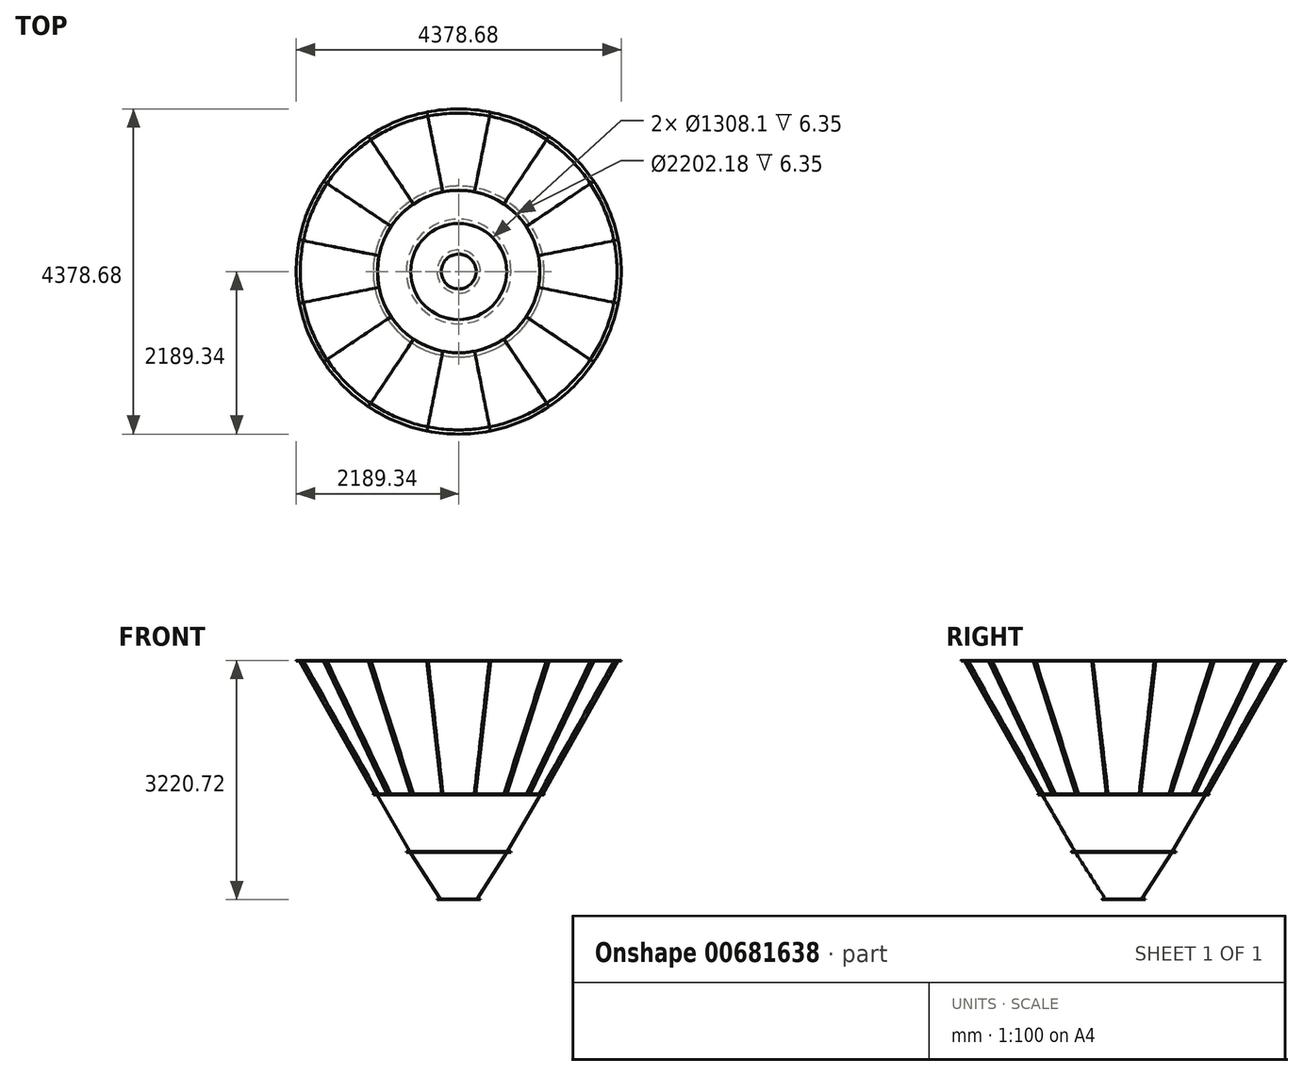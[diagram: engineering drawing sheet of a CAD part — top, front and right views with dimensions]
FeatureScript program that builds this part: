
annotation { "Feature Type Name" : "Feature", "Feature Type Description" : "" }
export const myFeature = defineFeature(function(context is Context, id is Id, definition is map)
    precondition{}
    {
        {
            var Q0;
            Q0=qCreatedBy(makeId("Top.planeOp"),FACE);
            var sketch = newSketch(context, id + "F0", { "sketchPlane" : qUnion([Q0])});
            skCircle(sketch, "E0", {"center": v(0, 0) * mm, "radius": 2133.6 * mm, "construction": true});
            skCircle(sketch, "E1", {"center": v(0, 0) * mm, "radius": 2139.95 * mm, "construction": true});
            skLineSegment(sketch, "E2", {"start": v(0, 0) * mm, "end": v(0, -2304.22) * mm});
            skLineSegment(sketch, "E3", {"start": v(0, -2304.22) * mm, "end": v(0, 0) * mm, "construction": true});
            skLineSegment(sketch, "E4", {"start": v(0, 0) * mm, "end": v(2542.21, 0) * mm, "construction": true});
            skLineSegment(sketch, "E5", {"start": v(0, 0) * mm, "end": v(1217.12, -1821.54) * mm, "construction": true});
            skLineSegment(sketch, "E6", {"start": v(0, 0) * mm, "end": v(1821.54, -1217.12) * mm, "construction": true});
            skLineSegment(sketch, "E7", {"start": v(1217.12, -1821.54) * mm, "end": v(1185.36, -1774.02) * mm});
            skLineSegment(sketch, "E8", {"start": v(1217.12, -1821.54) * mm, "end": v(1222.4, -1818.01) * mm});
            skLineSegment(sketch, "E9", {"start": v(1821.54, -1217.12) * mm, "end": v(1774.02, -1185.36) * mm});
            skLineSegment(sketch, "E10", {"start": v(1821.54, -1217.12) * mm, "end": v(1818.01, -1222.4) * mm});
            skArc(sketch, "E11", {"start": v(1185.36, -1774.02) * mm, "mid": v(1508.68, -1508.68) * mm, "end": v(1774.02, -1185.36) * mm});
            skLineSegment(sketch, "E12", {"start": v(1222.4, -1818.01) * mm, "end": v(1194.17, -1775.77) * mm});
            skLineSegment(sketch, "E13", {"start": v(1818.01, -1222.4) * mm, "end": v(1775.77, -1194.17) * mm});
            skArc(sketch, "E14", {"start": v(1194.17, -1775.77) * mm, "mid": v(1513.17, -1513.17) * mm, "end": v(1775.77, -1194.17) * mm});
            skLineSegment(sketch, "E15", {"start": v(0, 0) * mm, "end": v(2368.08, -471.04) * mm, "construction": true});
            skLineSegment(sketch, "E16", {"start": v(0, 0) * mm, "end": v(2425.64, 482.49) * mm, "construction": true});
            skLineSegment(sketch, "E17", {"start": v(0, 0) * mm, "end": v(2044.18, 1365.87) * mm, "construction": true});
            skLineSegment(sketch, "E18", {"start": v(0, 0) * mm, "end": v(1324.45, 1982.17) * mm, "construction": true});
            skLineSegment(sketch, "E19", {"start": v(0, 0) * mm, "end": v(473.22, 2379.02) * mm, "construction": true});
            skLineSegment(sketch, "E20", {"start": v(0, 0) * mm, "end": v(-472.95, 2377.66) * mm, "construction": true});
            skSolve(sketch);
        }
        {
            var Q0;
            Q0=qCreatedBy(makeId("Front.planeOp"),FACE);
            var sketch = newSketch(context, id + "F1", { "sketchPlane" : qUnion([Q0])});
            skLineSegment(sketch, "E21", {"start": v(0, 0) * mm, "end": v(0, -1803.4) * mm, "construction": true});
            skLineSegment(sketch, "E22", {"start": v(0, -1803.4) * mm, "end": v(0, -2578.1) * mm, "construction": true});
            skLineSegment(sketch, "E23", {"start": v(0, -2578.1) * mm, "end": v(0, -3220.72) * mm, "construction": true});
            skLineSegment(sketch, "E24", {"start": v(0, -1803.4) * mm, "end": v(-1101.72, -1803.4) * mm, "construction": true});
            skLineSegment(sketch, "E25", {"start": v(0, -1803.4) * mm, "end": v(1101.73, -1803.4) * mm, "construction": true});
            skLineSegment(sketch, "E26", {"start": v(0, -2578.1) * mm, "end": v(-475.6, -2578.1) * mm, "construction": true});
            skLineSegment(sketch, "E27", {"start": v(0, -3220.72) * mm, "end": v(-292.1, -3220.72) * mm, "construction": true});
            skSolve(sketch);
        }
        {
            var Q0;
            Q0=sQuery(id+"F1.wireOp",EDGE,"E25");
            cPlane(context, id + "F2", {"entities" : qUnion([Q0]), "cplaneType" : CPlaneType.LINE_ANGLE, "offset" : 25.4 * mm, "angle" : 90 * degree, "width" : 152.4 * mm, "height" : 152.4 * mm});
        }
        {
            var Q0;
            Q0=qCreatedBy(id+"F2.planeOp",FACE);
            var sketch = newSketch(context, id + "F3", { "sketchPlane" : qUnion([Q0])});
            skCircle(sketch, "E28", {"center": v(0, 0) * mm, "radius": 1151.9 * mm, "construction": true});
            skLineSegment(sketch, "E29", {"start": v(640.06, -957.7) * mm, "end": v(608.74, -911.75) * mm});
            skLineSegment(sketch, "E30", {"start": v(640.06, -957.7) * mm, "end": v(645.3, -954.12) * mm});
            skLineSegment(sketch, "E31", {"start": v(957.75, -639.98) * mm, "end": v(911.58, -609) * mm});
            skLineSegment(sketch, "E32", {"start": v(957.75, -639.98) * mm, "end": v(954.2, -645.6) * mm});
            skArc(sketch, "E33", {"start": v(608.74, -911.75) * mm, "mid": v(775.09, -775.3) * mm, "end": v(911.58, -609) * mm});
            skLineSegment(sketch, "E34", {"start": v(954.2, -645.6) * mm, "end": v(913.11, -618.03) * mm});
            skLineSegment(sketch, "E35", {"start": v(645.3, -954.12) * mm, "end": v(617.57, -913.42) * mm});
            skArc(sketch, "E36", {"start": v(617.57, -913.42) * mm, "mid": v(779.46, -779.85) * mm, "end": v(913.11, -618.03) * mm});
            skSolve(sketch);
        }
        {
            var Q0;
            Q0=makeQuery(id+"F3.imprint","IMPRINT",FACE,{"disambiguationData":[TD([[makeQuery(id+"F3.imprint","IMPRINT",EDGE,{"derivedFrom":sQuery(id+"F3.wireOp",EDGE,"E29")}),-1.0]])]});
            var Q1;
            Q1=makeQuery(id+"F0.imprint","IMPRINT",FACE,{"disambiguationData":[TD([[makeQuery(id+"F0.imprint","IMPRINT",EDGE,{"derivedFrom":sQuery(id+"F0.wireOp",EDGE,"E7")}),-1.0]])]});
            loft(context, id + "F4", {"sheetProfilesArray" : [{ "sheetProfileEntities" : qUnion([Q0]) }, { "sheetProfileEntities" : qUnion([Q1]) }]});
        }
        {
            var Q0;
            Q0=qCreatedBy(makeId("Top.planeOp"),FACE);
            var sketch = newSketch(context, id + "F5", { "sketchPlane" : qUnion([Q0])});
            skArc(sketch, "E37", {"start": v(1185.3, -1774.06) * mm, "mid": v(1508.65, -1508.72) * mm, "end": v(1774, -1185.39) * mm});
            skLineSegment(sketch, "E38", {"start": v(1185.3, -1774.06) * mm, "end": v(1216.33, -1820.37) * mm});
            skLineSegment(sketch, "E39", {"start": v(1774, -1185.39) * mm, "end": v(1820.44, -1216.23) * mm});
            skArc(sketch, "E40", {"start": v(1216.33, -1820.37) * mm, "mid": v(1548.14, -1548.05) * mm, "end": v(1820.44, -1216.23) * mm});
            skSolve(sketch);
        }
        {
            var Q0;
            Q0=makeQuery(id+"F5.imprint","IMPRINT",FACE,{"disambiguationData":[TD([[makeQuery(id+"F5.imprint","IMPRINT",EDGE,{"derivedFrom":sQuery(id+"F5.wireOp",EDGE,"E37")}),-1.0]])]});
            extrude(context, id + "F6", {"entities" : qUnion([Q0]), "operationType" : NewBodyOperationType.ADD, "oppositeDirection" : true, "depth" : 6.35 * mm, "offsetDistance" : 25.4 * mm});
        }
        {
            var Q0;
            Q0=qCreatedBy(id+"F2.planeOp",FACE);
            var sketch = newSketch(context, id + "F7", { "sketchPlane" : qUnion([Q0])});
            skArc(sketch, "E41", {"start": v(607.56, -909.75) * mm, "mid": v(773.48, -773.63) * mm, "end": v(909.63, -607.74) * mm});
            skArc(sketch, "E42", {"start": v(640.03, -957.7) * mm, "mid": v(814.54, -814.48) * mm, "end": v(957.76, -639.96) * mm});
            skLineSegment(sketch, "E43", {"start": v(607.56, -909.75) * mm, "end": v(640.03, -957.7) * mm});
            skLineSegment(sketch, "E44", {"start": v(909.63, -607.74) * mm, "end": v(957.76, -639.96) * mm});
            skSolve(sketch);
        }
        {
            var Q0;
            Q0 = qSketchRegion(id + "F7", true);
            extrude(context, id + "F8", {"entities" : qUnion([Q0]), "depth" : 6.35 * mm, "offsetDistance" : 25.4 * mm});
        }
        {
            var Q0;
            Q0=sQuery(id+"F0.wireOp",EDGE,"E5");
            cPlane(context, id + "F9", {"entities" : qUnion([Q0]), "cplaneType" : CPlaneType.LINE_ANGLE, "offset" : 25.4 * mm, "angle" : 90 * degree, "width" : 152.4 * mm, "height" : 152.4 * mm});
        }
        {
            var Q0;
            Q0=makeQuery(id+"F4.opLoft","SWEPT_BODY",BODY,{"disambiguationData":[OSD([makeQuery(id+"F0.imprint","IMPRINT",FACE,{"disambiguationData":[TD([[makeQuery(id+"F0.imprint","IMPRINT",EDGE,{"derivedFrom":sQuery(id+"F0.wireOp",EDGE,"E7")}),-1.0]])]}),makeQuery(id+"F3.imprint","IMPRINT",FACE,{"disambiguationData":[TD([[makeQuery(id+"F3.imprint","IMPRINT",EDGE,{"derivedFrom":sQuery(id+"F3.wireOp",EDGE,"E29")}),-1.0]])]})])]});
            var Q1;
            Q1=makeQuery(id+"F8.opExtrude","SWEPT_BODY",BODY,{"disambiguationData":[OSD([sQuery(id+"F7.wireOp",EDGE,"E41"),sQuery(id+"F7.wireOp",EDGE,"E42"),sQuery(id+"F7.wireOp",EDGE,"E43"),sQuery(id+"F7.wireOp",EDGE,"E44")])]});
            var Q2;
            Q2=qCreatedBy(id+"F9.planeOp",FACE);
            mirror(context, id + "F10", {"entities" : qUnion([Q0, Q1]), "mirrorPlane" : qUnion([Q2])});
        }
        {
            var Q0;
            Q0=sQuery(id+"F0.wireOp",EDGE,"E6");
            cPlane(context, id + "F11", {"entities" : qUnion([Q0]), "cplaneType" : CPlaneType.LINE_ANGLE, "offset" : 25.4 * mm, "angle" : 0 * degree, "width" : 152.4 * mm, "height" : 152.4 * mm});
        }
        {
            var Q0;
            Q0=makeQuery(id+"F4.opLoft","SWEPT_BODY",BODY,{"disambiguationData":[OSD([makeQuery(id+"F0.imprint","IMPRINT",FACE,{"disambiguationData":[TD([[makeQuery(id+"F0.imprint","IMPRINT",EDGE,{"derivedFrom":sQuery(id+"F0.wireOp",EDGE,"E7")}),-1.0]])]}),makeQuery(id+"F3.imprint","IMPRINT",FACE,{"disambiguationData":[TD([[makeQuery(id+"F3.imprint","IMPRINT",EDGE,{"derivedFrom":sQuery(id+"F3.wireOp",EDGE,"E29")}),-1.0]])]})])]});
            var Q1;
            Q1=makeQuery(id+"F8.opExtrude","SWEPT_BODY",BODY,{"disambiguationData":[OSD([sQuery(id+"F7.wireOp",EDGE,"E41"),sQuery(id+"F7.wireOp",EDGE,"E42"),sQuery(id+"F7.wireOp",EDGE,"E43"),sQuery(id+"F7.wireOp",EDGE,"E44")])]});
            var Q2;
            Q2=qCreatedBy(id+"F11.planeOp",FACE);
            mirror(context, id + "F12", {"entities" : qUnion([Q0, Q1]), "mirrorPlane" : qUnion([Q2])});
        }
        {
            var Q0;
            Q0=sQuery(id+"F0.wireOp",EDGE,"E15");
            cPlane(context, id + "F13", {"entities" : qUnion([Q0]), "cplaneType" : CPlaneType.LINE_ANGLE, "offset" : 25.4 * mm, "angle" : 0 * degree, "width" : 152.4 * mm, "height" : 152.4 * mm});
        }
        {
            var Q0;
            Q0=sQuery(id+"F0.wireOp",EDGE,"E16");
            cPlane(context, id + "F14", {"entities" : qUnion([Q0]), "cplaneType" : CPlaneType.LINE_ANGLE, "offset" : 25.4 * mm, "angle" : 0 * degree, "width" : 152.4 * mm, "height" : 152.4 * mm});
        }
        {
            var Q0;
            Q0=sQuery(id+"F0.wireOp",EDGE,"E17");
            cPlane(context, id + "F15", {"entities" : qUnion([Q0]), "cplaneType" : CPlaneType.LINE_ANGLE, "offset" : 25.4 * mm, "angle" : 0 * degree, "width" : 152.4 * mm, "height" : 152.4 * mm});
        }
        {
            var Q0;
            Q0=makeQuery(id+"F12.opPattern","COPY",BODY,{"derivedFrom":makeQuery(id+"F4.opLoft","SWEPT_BODY",BODY,{"disambiguationData":[OSD([makeQuery(id+"F0.imprint","IMPRINT",FACE,{"disambiguationData":[TD([[makeQuery(id+"F0.imprint","IMPRINT",EDGE,{"derivedFrom":sQuery(id+"F0.wireOp",EDGE,"E7")}),-1.0]])]}),makeQuery(id+"F3.imprint","IMPRINT",FACE,{"disambiguationData":[TD([[makeQuery(id+"F3.imprint","IMPRINT",EDGE,{"derivedFrom":sQuery(id+"F3.wireOp",EDGE,"E29")}),-1.0]])]})])]}),"instanceName":"1"});
            var Q1;
            Q1=makeQuery(id+"F12.opPattern","COPY",BODY,{"derivedFrom":makeQuery(id+"F8.opExtrude","SWEPT_BODY",BODY,{"disambiguationData":[OSD([sQuery(id+"F7.wireOp",EDGE,"E41"),sQuery(id+"F7.wireOp",EDGE,"E42"),sQuery(id+"F7.wireOp",EDGE,"E43"),sQuery(id+"F7.wireOp",EDGE,"E44")])]}),"instanceName":"1"});
            var Q2;
            Q2=qCreatedBy(id+"F13.planeOp",FACE);
            mirror(context, id + "F16", {"entities" : qUnion([Q0, Q1]), "mirrorPlane" : qUnion([Q2])});
        }
        {
            var Q0;
            Q0=makeQuery(id+"F16.opPattern","COPY",BODY,{"derivedFrom":makeQuery(id+"F12.opPattern","COPY",BODY,{"derivedFrom":makeQuery(id+"F4.opLoft","SWEPT_BODY",BODY,{"disambiguationData":[OSD([makeQuery(id+"F0.imprint","IMPRINT",FACE,{"disambiguationData":[TD([[makeQuery(id+"F0.imprint","IMPRINT",EDGE,{"derivedFrom":sQuery(id+"F0.wireOp",EDGE,"E7")}),-1.0]])]}),makeQuery(id+"F3.imprint","IMPRINT",FACE,{"disambiguationData":[TD([[makeQuery(id+"F3.imprint","IMPRINT",EDGE,{"derivedFrom":sQuery(id+"F3.wireOp",EDGE,"E29")}),-1.0]])]})])]}),"instanceName":"1"}),"instanceName":"1"});
            var Q1;
            Q1=makeQuery(id+"F16.opPattern","COPY",BODY,{"derivedFrom":makeQuery(id+"F12.opPattern","COPY",BODY,{"derivedFrom":makeQuery(id+"F8.opExtrude","SWEPT_BODY",BODY,{"disambiguationData":[OSD([sQuery(id+"F7.wireOp",EDGE,"E41"),sQuery(id+"F7.wireOp",EDGE,"E42"),sQuery(id+"F7.wireOp",EDGE,"E43"),sQuery(id+"F7.wireOp",EDGE,"E44")])]}),"instanceName":"1"}),"instanceName":"1"});
            var Q2;
            Q2=qCreatedBy(id+"F14.planeOp",FACE);
            mirror(context, id + "F17", {"entities" : qUnion([Q0, Q1]), "mirrorPlane" : qUnion([Q2])});
        }
        {
            var Q0;
            Q0=makeQuery(id+"F17.opPattern","COPY",BODY,{"derivedFrom":makeQuery(id+"F16.opPattern","COPY",BODY,{"derivedFrom":makeQuery(id+"F12.opPattern","COPY",BODY,{"derivedFrom":makeQuery(id+"F4.opLoft","SWEPT_BODY",BODY,{"disambiguationData":[OSD([makeQuery(id+"F0.imprint","IMPRINT",FACE,{"disambiguationData":[TD([[makeQuery(id+"F0.imprint","IMPRINT",EDGE,{"derivedFrom":sQuery(id+"F0.wireOp",EDGE,"E7")}),-1.0]])]}),makeQuery(id+"F3.imprint","IMPRINT",FACE,{"disambiguationData":[TD([[makeQuery(id+"F3.imprint","IMPRINT",EDGE,{"derivedFrom":sQuery(id+"F3.wireOp",EDGE,"E29")}),-1.0]])]})])]}),"instanceName":"1"}),"instanceName":"1"}),"instanceName":"1"});
            var Q1;
            Q1=makeQuery(id+"F17.opPattern","COPY",BODY,{"derivedFrom":makeQuery(id+"F16.opPattern","COPY",BODY,{"derivedFrom":makeQuery(id+"F12.opPattern","COPY",BODY,{"derivedFrom":makeQuery(id+"F8.opExtrude","SWEPT_BODY",BODY,{"disambiguationData":[OSD([sQuery(id+"F7.wireOp",EDGE,"E41"),sQuery(id+"F7.wireOp",EDGE,"E42"),sQuery(id+"F7.wireOp",EDGE,"E43"),sQuery(id+"F7.wireOp",EDGE,"E44")])]}),"instanceName":"1"}),"instanceName":"1"}),"instanceName":"1"});
            var Q2;
            Q2=qCreatedBy(id+"F15.planeOp",FACE);
            mirror(context, id + "F18", {"entities" : qUnion([Q0, Q1]), "mirrorPlane" : qUnion([Q2])});
        }
        {
            var Q0;
            Q0=sQuery(id+"F0.wireOp",EDGE,"E18");
            cPlane(context, id + "F19", {"entities" : qUnion([Q0]), "cplaneType" : CPlaneType.LINE_ANGLE, "offset" : 25.4 * mm, "angle" : 90 * degree, "width" : 152.4 * mm, "height" : 152.4 * mm});
        }
        {
            var Q0;
            Q0=sQuery(id+"F0.wireOp",EDGE,"E19");
            cPlane(context, id + "F20", {"entities" : qUnion([Q0]), "cplaneType" : CPlaneType.LINE_ANGLE, "offset" : 25.4 * mm, "angle" : 90 * degree, "width" : 152.4 * mm, "height" : 152.4 * mm});
        }
        {
            var Q0;
            Q0=sQuery(id+"F0.wireOp",EDGE,"E20");
            cPlane(context, id + "F21", {"entities" : qUnion([Q0]), "cplaneType" : CPlaneType.LINE_ANGLE, "offset" : 25.4 * mm, "angle" : 90 * degree, "width" : 152.4 * mm, "height" : 152.4 * mm});
        }
        {
            var Q0;
            Q0=makeQuery(id+"F18.opPattern","COPY",BODY,{"derivedFrom":makeQuery(id+"F17.opPattern","COPY",BODY,{"derivedFrom":makeQuery(id+"F16.opPattern","COPY",BODY,{"derivedFrom":makeQuery(id+"F12.opPattern","COPY",BODY,{"derivedFrom":makeQuery(id+"F4.opLoft","SWEPT_BODY",BODY,{"disambiguationData":[OSD([makeQuery(id+"F0.imprint","IMPRINT",FACE,{"disambiguationData":[TD([[makeQuery(id+"F0.imprint","IMPRINT",EDGE,{"derivedFrom":sQuery(id+"F0.wireOp",EDGE,"E7")}),-1.0]])]}),makeQuery(id+"F3.imprint","IMPRINT",FACE,{"disambiguationData":[TD([[makeQuery(id+"F3.imprint","IMPRINT",EDGE,{"derivedFrom":sQuery(id+"F3.wireOp",EDGE,"E29")}),-1.0]])]})])]}),"instanceName":"1"}),"instanceName":"1"}),"instanceName":"1"}),"instanceName":"1"});
            var Q1;
            Q1=makeQuery(id+"F18.opPattern","COPY",BODY,{"derivedFrom":makeQuery(id+"F17.opPattern","COPY",BODY,{"derivedFrom":makeQuery(id+"F16.opPattern","COPY",BODY,{"derivedFrom":makeQuery(id+"F12.opPattern","COPY",BODY,{"derivedFrom":makeQuery(id+"F8.opExtrude","SWEPT_BODY",BODY,{"disambiguationData":[OSD([sQuery(id+"F7.wireOp",EDGE,"E41"),sQuery(id+"F7.wireOp",EDGE,"E42"),sQuery(id+"F7.wireOp",EDGE,"E43"),sQuery(id+"F7.wireOp",EDGE,"E44")])]}),"instanceName":"1"}),"instanceName":"1"}),"instanceName":"1"}),"instanceName":"1"});
            var Q2;
            Q2=qCreatedBy(id+"F19.planeOp",FACE);
            mirror(context, id + "F22", {"entities" : qUnion([Q0, Q1]), "mirrorPlane" : qUnion([Q2])});
        }
        {
            var Q0;
            Q0=makeQuery(id+"F22.opPattern","COPY",BODY,{"derivedFrom":makeQuery(id+"F18.opPattern","COPY",BODY,{"derivedFrom":makeQuery(id+"F17.opPattern","COPY",BODY,{"derivedFrom":makeQuery(id+"F16.opPattern","COPY",BODY,{"derivedFrom":makeQuery(id+"F12.opPattern","COPY",BODY,{"derivedFrom":makeQuery(id+"F4.opLoft","SWEPT_BODY",BODY,{"disambiguationData":[OSD([makeQuery(id+"F0.imprint","IMPRINT",FACE,{"disambiguationData":[TD([[makeQuery(id+"F0.imprint","IMPRINT",EDGE,{"derivedFrom":sQuery(id+"F0.wireOp",EDGE,"E7")}),-1.0]])]}),makeQuery(id+"F3.imprint","IMPRINT",FACE,{"disambiguationData":[TD([[makeQuery(id+"F3.imprint","IMPRINT",EDGE,{"derivedFrom":sQuery(id+"F3.wireOp",EDGE,"E29")}),-1.0]])]})])]}),"instanceName":"1"}),"instanceName":"1"}),"instanceName":"1"}),"instanceName":"1"}),"instanceName":"1"});
            var Q1;
            Q1=makeQuery(id+"F22.opPattern","COPY",BODY,{"derivedFrom":makeQuery(id+"F18.opPattern","COPY",BODY,{"derivedFrom":makeQuery(id+"F17.opPattern","COPY",BODY,{"derivedFrom":makeQuery(id+"F16.opPattern","COPY",BODY,{"derivedFrom":makeQuery(id+"F12.opPattern","COPY",BODY,{"derivedFrom":makeQuery(id+"F8.opExtrude","SWEPT_BODY",BODY,{"disambiguationData":[OSD([sQuery(id+"F7.wireOp",EDGE,"E41"),sQuery(id+"F7.wireOp",EDGE,"E42"),sQuery(id+"F7.wireOp",EDGE,"E43"),sQuery(id+"F7.wireOp",EDGE,"E44")])]}),"instanceName":"1"}),"instanceName":"1"}),"instanceName":"1"}),"instanceName":"1"}),"instanceName":"1"});
            var Q2;
            Q2=qCreatedBy(id+"F20.planeOp",FACE);
            mirror(context, id + "F23", {"entities" : qUnion([Q0, Q1]), "mirrorPlane" : qUnion([Q2])});
        }
        {
            var Q0;
            Q0=makeQuery(id+"F23.opPattern","COPY",BODY,{"derivedFrom":makeQuery(id+"F22.opPattern","COPY",BODY,{"derivedFrom":makeQuery(id+"F18.opPattern","COPY",BODY,{"derivedFrom":makeQuery(id+"F17.opPattern","COPY",BODY,{"derivedFrom":makeQuery(id+"F16.opPattern","COPY",BODY,{"derivedFrom":makeQuery(id+"F12.opPattern","COPY",BODY,{"derivedFrom":makeQuery(id+"F4.opLoft","SWEPT_BODY",BODY,{"disambiguationData":[OSD([makeQuery(id+"F0.imprint","IMPRINT",FACE,{"disambiguationData":[TD([[makeQuery(id+"F0.imprint","IMPRINT",EDGE,{"derivedFrom":sQuery(id+"F0.wireOp",EDGE,"E7")}),-1.0]])]}),makeQuery(id+"F3.imprint","IMPRINT",FACE,{"disambiguationData":[TD([[makeQuery(id+"F3.imprint","IMPRINT",EDGE,{"derivedFrom":sQuery(id+"F3.wireOp",EDGE,"E29")}),-1.0]])]})])]}),"instanceName":"1"}),"instanceName":"1"}),"instanceName":"1"}),"instanceName":"1"}),"instanceName":"1"}),"instanceName":"1"});
            var Q1;
            Q1=makeQuery(id+"F22.opPattern","COPY",BODY,{"derivedFrom":makeQuery(id+"F18.opPattern","COPY",BODY,{"derivedFrom":makeQuery(id+"F17.opPattern","COPY",BODY,{"derivedFrom":makeQuery(id+"F16.opPattern","COPY",BODY,{"derivedFrom":makeQuery(id+"F12.opPattern","COPY",BODY,{"derivedFrom":makeQuery(id+"F4.opLoft","SWEPT_BODY",BODY,{"disambiguationData":[OSD([makeQuery(id+"F0.imprint","IMPRINT",FACE,{"disambiguationData":[TD([[makeQuery(id+"F0.imprint","IMPRINT",EDGE,{"derivedFrom":sQuery(id+"F0.wireOp",EDGE,"E7")}),-1.0]])]}),makeQuery(id+"F3.imprint","IMPRINT",FACE,{"disambiguationData":[TD([[makeQuery(id+"F3.imprint","IMPRINT",EDGE,{"derivedFrom":sQuery(id+"F3.wireOp",EDGE,"E29")}),-1.0]])]})])]}),"instanceName":"1"}),"instanceName":"1"}),"instanceName":"1"}),"instanceName":"1"}),"instanceName":"1"});
            var Q2;
            Q2=makeQuery(id+"F18.opPattern","COPY",BODY,{"derivedFrom":makeQuery(id+"F17.opPattern","COPY",BODY,{"derivedFrom":makeQuery(id+"F16.opPattern","COPY",BODY,{"derivedFrom":makeQuery(id+"F12.opPattern","COPY",BODY,{"derivedFrom":makeQuery(id+"F4.opLoft","SWEPT_BODY",BODY,{"disambiguationData":[OSD([makeQuery(id+"F0.imprint","IMPRINT",FACE,{"disambiguationData":[TD([[makeQuery(id+"F0.imprint","IMPRINT",EDGE,{"derivedFrom":sQuery(id+"F0.wireOp",EDGE,"E7")}),-1.0]])]}),makeQuery(id+"F3.imprint","IMPRINT",FACE,{"disambiguationData":[TD([[makeQuery(id+"F3.imprint","IMPRINT",EDGE,{"derivedFrom":sQuery(id+"F3.wireOp",EDGE,"E29")}),-1.0]])]})])]}),"instanceName":"1"}),"instanceName":"1"}),"instanceName":"1"}),"instanceName":"1"});
            var Q3;
            Q3=makeQuery(id+"F17.opPattern","COPY",BODY,{"derivedFrom":makeQuery(id+"F16.opPattern","COPY",BODY,{"derivedFrom":makeQuery(id+"F12.opPattern","COPY",BODY,{"derivedFrom":makeQuery(id+"F4.opLoft","SWEPT_BODY",BODY,{"disambiguationData":[OSD([makeQuery(id+"F0.imprint","IMPRINT",FACE,{"disambiguationData":[TD([[makeQuery(id+"F0.imprint","IMPRINT",EDGE,{"derivedFrom":sQuery(id+"F0.wireOp",EDGE,"E7")}),-1.0]])]}),makeQuery(id+"F3.imprint","IMPRINT",FACE,{"disambiguationData":[TD([[makeQuery(id+"F3.imprint","IMPRINT",EDGE,{"derivedFrom":sQuery(id+"F3.wireOp",EDGE,"E29")}),-1.0]])]})])]}),"instanceName":"1"}),"instanceName":"1"}),"instanceName":"1"});
            var Q4;
            Q4=makeQuery(id+"F16.opPattern","COPY",BODY,{"derivedFrom":makeQuery(id+"F12.opPattern","COPY",BODY,{"derivedFrom":makeQuery(id+"F4.opLoft","SWEPT_BODY",BODY,{"disambiguationData":[OSD([makeQuery(id+"F0.imprint","IMPRINT",FACE,{"disambiguationData":[TD([[makeQuery(id+"F0.imprint","IMPRINT",EDGE,{"derivedFrom":sQuery(id+"F0.wireOp",EDGE,"E7")}),-1.0]])]}),makeQuery(id+"F3.imprint","IMPRINT",FACE,{"disambiguationData":[TD([[makeQuery(id+"F3.imprint","IMPRINT",EDGE,{"derivedFrom":sQuery(id+"F3.wireOp",EDGE,"E29")}),-1.0]])]})])]}),"instanceName":"1"}),"instanceName":"1"});
            var Q5;
            Q5=makeQuery(id+"F12.opPattern","COPY",BODY,{"derivedFrom":makeQuery(id+"F4.opLoft","SWEPT_BODY",BODY,{"disambiguationData":[OSD([makeQuery(id+"F0.imprint","IMPRINT",FACE,{"disambiguationData":[TD([[makeQuery(id+"F0.imprint","IMPRINT",EDGE,{"derivedFrom":sQuery(id+"F0.wireOp",EDGE,"E7")}),-1.0]])]}),makeQuery(id+"F3.imprint","IMPRINT",FACE,{"disambiguationData":[TD([[makeQuery(id+"F3.imprint","IMPRINT",EDGE,{"derivedFrom":sQuery(id+"F3.wireOp",EDGE,"E29")}),-1.0]])]})])]}),"instanceName":"1"});
            var Q6;
            Q6=makeQuery(id+"F4.opLoft","SWEPT_BODY",BODY,{"disambiguationData":[OSD([makeQuery(id+"F0.imprint","IMPRINT",FACE,{"disambiguationData":[TD([[makeQuery(id+"F0.imprint","IMPRINT",EDGE,{"derivedFrom":sQuery(id+"F0.wireOp",EDGE,"E7")}),-1.0]])]}),makeQuery(id+"F3.imprint","IMPRINT",FACE,{"disambiguationData":[TD([[makeQuery(id+"F3.imprint","IMPRINT",EDGE,{"derivedFrom":sQuery(id+"F3.wireOp",EDGE,"E29")}),-1.0]])]})])]});
            var Q7;
            Q7=makeQuery(id+"F10.opPattern","COPY",BODY,{"derivedFrom":makeQuery(id+"F4.opLoft","SWEPT_BODY",BODY,{"disambiguationData":[OSD([makeQuery(id+"F0.imprint","IMPRINT",FACE,{"disambiguationData":[TD([[makeQuery(id+"F0.imprint","IMPRINT",EDGE,{"derivedFrom":sQuery(id+"F0.wireOp",EDGE,"E7")}),-1.0]])]}),makeQuery(id+"F3.imprint","IMPRINT",FACE,{"disambiguationData":[TD([[makeQuery(id+"F3.imprint","IMPRINT",EDGE,{"derivedFrom":sQuery(id+"F3.wireOp",EDGE,"E29")}),-1.0]])]})])]}),"instanceName":"1"});
            var Q8;
            Q8=makeQuery(id+"F10.opPattern","COPY",BODY,{"derivedFrom":makeQuery(id+"F8.opExtrude","SWEPT_BODY",BODY,{"disambiguationData":[OSD([sQuery(id+"F7.wireOp",EDGE,"E41"),sQuery(id+"F7.wireOp",EDGE,"E42"),sQuery(id+"F7.wireOp",EDGE,"E43"),sQuery(id+"F7.wireOp",EDGE,"E44")])]}),"instanceName":"1"});
            var Q9;
            Q9=makeQuery(id+"F8.opExtrude","SWEPT_BODY",BODY,{"disambiguationData":[OSD([sQuery(id+"F7.wireOp",EDGE,"E41"),sQuery(id+"F7.wireOp",EDGE,"E42"),sQuery(id+"F7.wireOp",EDGE,"E43"),sQuery(id+"F7.wireOp",EDGE,"E44")])]});
            var Q10;
            Q10=makeQuery(id+"F12.opPattern","COPY",BODY,{"derivedFrom":makeQuery(id+"F8.opExtrude","SWEPT_BODY",BODY,{"disambiguationData":[OSD([sQuery(id+"F7.wireOp",EDGE,"E41"),sQuery(id+"F7.wireOp",EDGE,"E42"),sQuery(id+"F7.wireOp",EDGE,"E43"),sQuery(id+"F7.wireOp",EDGE,"E44")])]}),"instanceName":"1"});
            var Q11;
            Q11=makeQuery(id+"F16.opPattern","COPY",BODY,{"derivedFrom":makeQuery(id+"F12.opPattern","COPY",BODY,{"derivedFrom":makeQuery(id+"F8.opExtrude","SWEPT_BODY",BODY,{"disambiguationData":[OSD([sQuery(id+"F7.wireOp",EDGE,"E41"),sQuery(id+"F7.wireOp",EDGE,"E42"),sQuery(id+"F7.wireOp",EDGE,"E43"),sQuery(id+"F7.wireOp",EDGE,"E44")])]}),"instanceName":"1"}),"instanceName":"1"});
            var Q12;
            Q12=makeQuery(id+"F17.opPattern","COPY",BODY,{"derivedFrom":makeQuery(id+"F16.opPattern","COPY",BODY,{"derivedFrom":makeQuery(id+"F12.opPattern","COPY",BODY,{"derivedFrom":makeQuery(id+"F8.opExtrude","SWEPT_BODY",BODY,{"disambiguationData":[OSD([sQuery(id+"F7.wireOp",EDGE,"E41"),sQuery(id+"F7.wireOp",EDGE,"E42"),sQuery(id+"F7.wireOp",EDGE,"E43"),sQuery(id+"F7.wireOp",EDGE,"E44")])]}),"instanceName":"1"}),"instanceName":"1"}),"instanceName":"1"});
            var Q13;
            Q13=makeQuery(id+"F18.opPattern","COPY",BODY,{"derivedFrom":makeQuery(id+"F17.opPattern","COPY",BODY,{"derivedFrom":makeQuery(id+"F16.opPattern","COPY",BODY,{"derivedFrom":makeQuery(id+"F12.opPattern","COPY",BODY,{"derivedFrom":makeQuery(id+"F8.opExtrude","SWEPT_BODY",BODY,{"disambiguationData":[OSD([sQuery(id+"F7.wireOp",EDGE,"E41"),sQuery(id+"F7.wireOp",EDGE,"E42"),sQuery(id+"F7.wireOp",EDGE,"E43"),sQuery(id+"F7.wireOp",EDGE,"E44")])]}),"instanceName":"1"}),"instanceName":"1"}),"instanceName":"1"}),"instanceName":"1"});
            var Q14;
            Q14=makeQuery(id+"F22.opPattern","COPY",BODY,{"derivedFrom":makeQuery(id+"F18.opPattern","COPY",BODY,{"derivedFrom":makeQuery(id+"F17.opPattern","COPY",BODY,{"derivedFrom":makeQuery(id+"F16.opPattern","COPY",BODY,{"derivedFrom":makeQuery(id+"F12.opPattern","COPY",BODY,{"derivedFrom":makeQuery(id+"F8.opExtrude","SWEPT_BODY",BODY,{"disambiguationData":[OSD([sQuery(id+"F7.wireOp",EDGE,"E41"),sQuery(id+"F7.wireOp",EDGE,"E42"),sQuery(id+"F7.wireOp",EDGE,"E43"),sQuery(id+"F7.wireOp",EDGE,"E44")])]}),"instanceName":"1"}),"instanceName":"1"}),"instanceName":"1"}),"instanceName":"1"}),"instanceName":"1"});
            var Q15;
            Q15=makeQuery(id+"F23.opPattern","COPY",BODY,{"derivedFrom":makeQuery(id+"F22.opPattern","COPY",BODY,{"derivedFrom":makeQuery(id+"F18.opPattern","COPY",BODY,{"derivedFrom":makeQuery(id+"F17.opPattern","COPY",BODY,{"derivedFrom":makeQuery(id+"F16.opPattern","COPY",BODY,{"derivedFrom":makeQuery(id+"F12.opPattern","COPY",BODY,{"derivedFrom":makeQuery(id+"F8.opExtrude","SWEPT_BODY",BODY,{"disambiguationData":[OSD([sQuery(id+"F7.wireOp",EDGE,"E41"),sQuery(id+"F7.wireOp",EDGE,"E42"),sQuery(id+"F7.wireOp",EDGE,"E43"),sQuery(id+"F7.wireOp",EDGE,"E44")])]}),"instanceName":"1"}),"instanceName":"1"}),"instanceName":"1"}),"instanceName":"1"}),"instanceName":"1"}),"instanceName":"1"});
            var Q16;
            Q16=qCreatedBy(id+"F21.planeOp",FACE);
            mirror(context, id + "F24", {"entities" : qUnion([Q0, Q1, Q2, Q3, Q4, Q5, Q6, Q7, Q8, Q9, Q10, Q11, Q12, Q13, Q14, Q15]), "mirrorPlane" : qUnion([Q16])});
        }
        {
            var Q0;
            Q0=sQuery(id+"F1.wireOp",EDGE,"E26");
            cPlane(context, id + "F25", {"entities" : qUnion([Q0]), "cplaneType" : CPlaneType.LINE_ANGLE, "offset" : 25.4 * mm, "angle" : 90 * degree, "width" : 152.4 * mm, "height" : 152.4 * mm});
        }
        {
            var Q0;
            Q0=sQuery(id+"F1.wireOp",EDGE,"E27");
            cPlane(context, id + "F26", {"entities" : qUnion([Q0]), "cplaneType" : CPlaneType.LINE_ANGLE, "offset" : 25.4 * mm, "angle" : 90 * degree, "width" : 152.4 * mm, "height" : 152.4 * mm});
        }
        {
            var Q0;
            Q0=qCreatedBy(id+"F25.planeOp",FACE);
            var sketch = newSketch(context, id + "F27", { "sketchPlane" : qUnion([Q0])});
            skCircle(sketch, "E45", {"center": v(0, 0) * mm, "radius": 704.85 * mm});
            skCircle(sketch, "E46", {"center": v(0, 0) * mm, "radius": 647.7 * mm});
            skCircle(sketch, "E47", {"center": v(0, 0) * mm, "radius": 654.05 * mm});
            skSolve(sketch);
        }
        {
            var Q0;
            Q0 = qSketchRegion(id + "F7", true);
            extrude(context, id + "F28", {"entities" : qUnion([Q0]), "depth" : 6.35 * mm, "offsetDistance" : 25.4 * mm});
        }
        {
            var Q0;
            Q0=qCreatedBy(id+"F2.planeOp",FACE);
            var sketch = newSketch(context, id + "F29", { "sketchPlane" : qUnion([Q0])});
            skCircle(sketch, "E48", {"center": v(0, 0) * mm, "radius": 1151.9 * mm});
            skCircle(sketch, "E49", {"center": v(0, 0) * mm, "radius": 1101.1 * mm});
            skCircle(sketch, "E50", {"center": v(0, 0) * mm, "radius": 1094.74 * mm});
            skSolve(sketch);
        }
        {
            var Q0;
            Q0=makeQuery(id+"F29.imprint","IMPRINT",FACE,{"disambiguationData":[TD([[makeQuery(id+"F29.imprint","IMPRINT",EDGE,{"derivedFrom":sQuery(id+"F29.wireOp",EDGE,"E48")}),1.0]])]});
            extrude(context, id + "F30", {"entities" : qUnion([Q0]), "oppositeDirection" : true, "depth" : 6.35 * mm, "offsetDistance" : 25.4 * mm});
        }
        {
            var Q0;
            Q0=makeQuery(id+"F27.imprint","IMPRINT",FACE,{"disambiguationData":[TD([[makeQuery(id+"F27.imprint","IMPRINT",EDGE,{"derivedFrom":sQuery(id+"F27.wireOp",EDGE,"E45")}),1.0]])]});
            extrude(context, id + "F31", {"entities" : qUnion([Q0]), "depth" : 6.35 * mm, "offsetDistance" : 25.4 * mm});
        }
        {
            var Q0;
            Q0=qCreatedBy(id+"F2.planeOp",FACE);
            var sketch = newSketch(context, id + "F32", { "sketchPlane" : qUnion([Q0])});
            skCircle(sketch, "E51", {"center": v(0, 0) * mm, "radius": 1101.1 * mm});
            skSolve(sketch);
        }
        {
            var Q0;
            Q0=qCreatedBy(id+"F25.planeOp",FACE);
            var sketch = newSketch(context, id + "F33", { "sketchPlane" : qUnion([Q0])});
            skCircle(sketch, "E52", {"center": v(0, 0) * mm, "radius": 654.05 * mm});
            skSolve(sketch);
        }
        {
            var Q0;
            Q0=makeQuery(id+"F33.imprint","IMPRINT",FACE,{"disambiguationData":[TD([[makeQuery(id+"F33.imprint","IMPRINT",EDGE,{"derivedFrom":sQuery(id+"F33.wireOp",EDGE,"E52")}),1.0]])]});
            var Q1;
            Q1=makeQuery(id+"F32.imprint","IMPRINT",FACE,{"disambiguationData":[TD([[makeQuery(id+"F32.imprint","IMPRINT",EDGE,{"derivedFrom":sQuery(id+"F32.wireOp",EDGE,"E51")}),1.0]])]});
            loft(context, id + "F34", {"sheetProfilesArray" : [{ "sheetProfileEntities" : qUnion([Q0]) }, { "sheetProfileEntities" : qUnion([Q1]) }]});
        }
        {
            var Q0;
            Q0=makeQuery(id+"F34.opLoft","CAP_FACE",FACE,{"disambiguationData":[OSD([makeQuery(id+"F33.imprint","IMPRINT",FACE,{"disambiguationData":[TD([[makeQuery(id+"F33.imprint","IMPRINT",EDGE,{"derivedFrom":sQuery(id+"F33.wireOp",EDGE,"E52")}),1.0]])]})])],"isStart":true});
            var Q1;
            Q1=makeQuery(id+"F34.opLoft","CAP_FACE",FACE,{"disambiguationData":[OSD([makeQuery(id+"F32.imprint","IMPRINT",FACE,{"disambiguationData":[TD([[makeQuery(id+"F32.imprint","IMPRINT",EDGE,{"derivedFrom":sQuery(id+"F32.wireOp",EDGE,"E51")}),1.0]])]})])],"isStart":true});
            shell(context, id + "F35", {"entities" : qUnion([Q0, Q1]), "thickness" : 6.35 * mm});
        }
        {
            var Q0;
            Q0=qCreatedBy(id+"F25.planeOp",FACE);
            var sketch = newSketch(context, id + "F36", { "sketchPlane" : qUnion([Q0])});
            skCircle(sketch, "E53", {"center": v(0, 0) * mm, "radius": 704.85 * mm});
            skCircle(sketch, "E54", {"center": v(0, 0) * mm, "radius": 654.05 * mm});
            skSolve(sketch);
        }
        {
            var Q0;
            Q0=qCreatedBy(id+"F26.planeOp",FACE);
            var sketch = newSketch(context, id + "F37", { "sketchPlane" : qUnion([Q0])});
            skCircle(sketch, "E55", {"center": v(0, 0) * mm, "radius": 292.1 * mm});
            skCircle(sketch, "E56", {"center": v(0, 0) * mm, "radius": 241.3 * mm});
            skSolve(sketch);
        }
        {
            var Q0;
            Q0=makeQuery(id+"F36.imprint","IMPRINT",FACE,{"disambiguationData":[TD([[makeQuery(id+"F36.imprint","IMPRINT",EDGE,{"derivedFrom":sQuery(id+"F36.wireOp",EDGE,"E53")}),1.0]])]});
            cPlane(context, id + "F38", {"entities" : qUnion([Q0]), "cplaneType" : CPlaneType.OFFSET, "offset" : 0.5 * mm, "oppositeDirection" : true, "width" : 152.4 * mm, "height" : 152.4 * mm});
        }
        {
            var Q0;
            Q0=makeQuery(id+"F36.imprint","IMPRINT",FACE,{"disambiguationData":[TD([[makeQuery(id+"F36.imprint","IMPRINT",EDGE,{"derivedFrom":sQuery(id+"F36.wireOp",EDGE,"E53")}),1.0]])]});
            extrude(context, id + "F39", {"entities" : qUnion([Q0]), "oppositeDirection" : true, "depth" : 6.35 * mm, "hasOffset" : true, "offsetDistance" : 25.4 * mm, "offsetOppositeDirection" : true});
        }
        {
            var Q0;
            Q0=makeQuery(id+"F37.imprint","IMPRINT",FACE,{"disambiguationData":[TD([[makeQuery(id+"F37.imprint","IMPRINT",EDGE,{"derivedFrom":sQuery(id+"F37.wireOp",EDGE,"E55")}),1.0]])]});
            extrude(context, id + "F40", {"entities" : qUnion([Q0]), "depth" : 6.35 * mm, "offsetDistance" : 25.4 * mm});
        }
        {
            var Q0;
            Q0=qCreatedBy(id+"F38.planeOp",FACE);
            var sketch = newSketch(context, id + "F41", { "sketchPlane" : qUnion([Q0])});
            skCircle(sketch, "E57", {"center": v(0, 0) * mm, "radius": 654.05 * mm});
            skSolve(sketch);
        }
        {
            var Q0;
            Q0=qCreatedBy(id+"F26.planeOp",FACE);
            var sketch = newSketch(context, id + "F42", { "sketchPlane" : qUnion([Q0])});
            skCircle(sketch, "E58", {"center": v(0, 0) * mm, "radius": 241.3 * mm});
            skSolve(sketch);
        }
        {
            var Q1;
            Q1=makeQuery(id+"F41.imprint","IMPRINT",FACE,{"disambiguationData":[TD([[makeQuery(id+"F41.imprint","IMPRINT",EDGE,{"derivedFrom":sQuery(id+"F41.wireOp",EDGE,"E57")}),1.0]])]});
            var Q2;
            Q2=makeQuery(id+"F42.imprint","IMPRINT",FACE,{"disambiguationData":[TD([[makeQuery(id+"F42.imprint","IMPRINT",EDGE,{"derivedFrom":sQuery(id+"F42.wireOp",EDGE,"E58")}),1.0]])]});
            loft(context, id + "F43", {"operationType" : NewBodyOperationType.ADD, "sheetProfilesArray" : [{ "sheetProfileEntities" : qUnion([Q1]) }, { "sheetProfileEntities" : qUnion([Q2]) }]});
        }
        {
            var Q0;
            Q0=makeQuery(id+"F43.opLoft","CAP_FACE",FACE,{"disambiguationData":[OSD([makeQuery(id+"F41.imprint","IMPRINT",FACE,{"disambiguationData":[TD([[makeQuery(id+"F41.imprint","IMPRINT",EDGE,{"derivedFrom":sQuery(id+"F41.wireOp",EDGE,"E57")}),1.0]])]})])],"isStart":true});
            var Q1;
            Q1=makeQuery(id+"F43.boolean.opBoolean","MERGE",FACE,{"derivedFrom":[makeQuery(id+"F40.opExtrude","CAP_FACE",FACE,{"disambiguationData":[OSD([sQuery(id+"F37.wireOp",EDGE,"E55"),sQuery(id+"F37.wireOp",EDGE,"E56")])],"isStart":true}),makeQuery(id+"F43.opLoft","CAP_FACE",FACE,{"disambiguationData":[OSD([makeQuery(id+"F42.imprint","IMPRINT",FACE,{"disambiguationData":[TD([[makeQuery(id+"F42.imprint","IMPRINT",EDGE,{"derivedFrom":sQuery(id+"F42.wireOp",EDGE,"E58")}),1.0]])]})])],"isStart":true})]});
            shell(context, id + "F44", {"entities" : qUnion([Q0, Q1]), "thickness" : 6.35 * mm});
        }
    });
